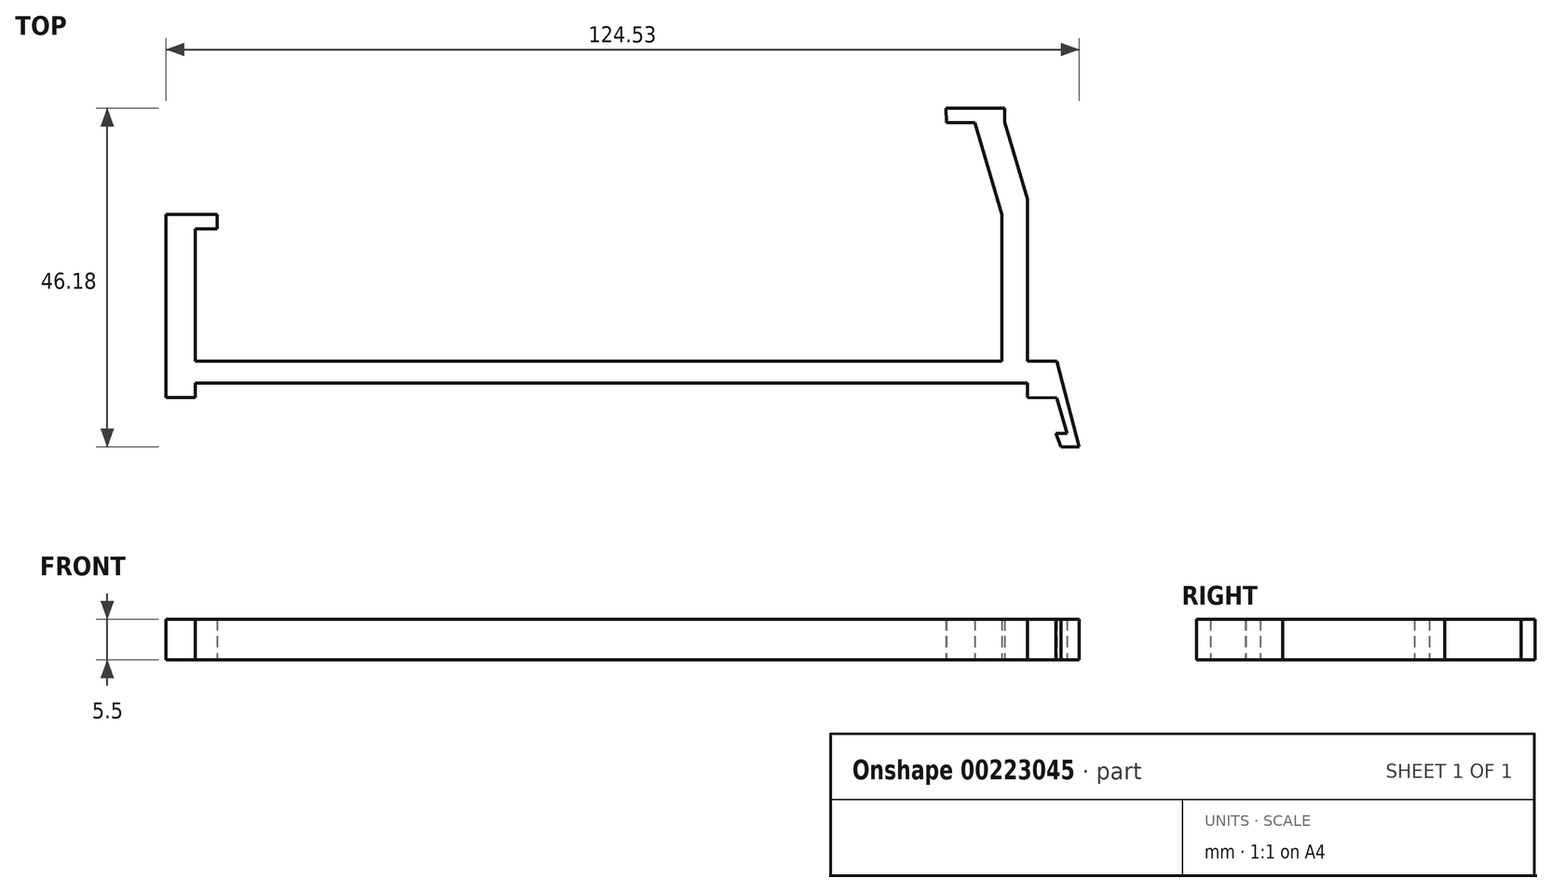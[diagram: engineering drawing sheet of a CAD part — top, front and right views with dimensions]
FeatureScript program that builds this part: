
annotation { "Feature Type Name" : "Feature", "Feature Type Description" : "" }
export const myFeature = defineFeature(function(context is Context, id is Id, definition is map)
    precondition{}
    {
        {
            var Q0;
            Q0=qCreatedBy(makeId("Top.planeOp"),FACE);
            var sketch = newSketch(context, id + "F0", { "sketchPlane" : qUnion([Q0])});
            skLineSegment(sketch, "E0.bottom", {"start": v(-40.4, -50.42) * mm, "end": v(-36.4, -50.42) * mm});
            skLineSegment(sketch, "E0.top", {"start": v(-40.4, -73.42) * mm, "end": v(-36.4, -73.42) * mm});
            skLineSegment(sketch, "E0.left", {"start": v(-40.4, -50.42) * mm, "end": v(-40.4, -73.42) * mm});
            skLineSegment(sketch, "E0.right", {"start": v(-36.4, -50.42) * mm, "end": v(-36.4, -73.42) * mm});
            skLineSegment(sketch, "E1.bottom", {"start": v(-36.4, -73.42) * mm, "end": v(77.03, -73.42) * mm});
            skLineSegment(sketch, "E1.top", {"start": v(-36.4, -70.42) * mm, "end": v(77.03, -70.42) * mm});
            skLineSegment(sketch, "E1.left", {"start": v(-36.4, -73.42) * mm, "end": v(-36.4, -70.42) * mm});
            skLineSegment(sketch, "E1.right", {"start": v(77.03, -73.42) * mm, "end": v(77.03, -70.42) * mm});
            skLineSegment(sketch, "E2.top", {"start": v(-40.4, -75.42) * mm, "end": v(-36.4, -75.42) * mm});
            skLineSegment(sketch, "E2.left", {"start": v(-40.4, -73.42) * mm, "end": v(-40.4, -75.42) * mm});
            skLineSegment(sketch, "E2.right", {"start": v(-36.4, -73.42) * mm, "end": v(-36.4, -75.42) * mm});
            skLineSegment(sketch, "E3.bottom", {"start": v(-36.4, -50.42) * mm, "end": v(-33.4, -50.42) * mm});
            skLineSegment(sketch, "E3.top", {"start": v(-36.4, -52.42) * mm, "end": v(-33.4, -52.42) * mm});
            skLineSegment(sketch, "E3.left", {"start": v(-36.4, -50.42) * mm, "end": v(-36.4, -52.42) * mm});
            skLineSegment(sketch, "E3.right", {"start": v(-33.4, -50.42) * mm, "end": v(-33.4, -52.42) * mm});
            skLineSegment(sketch, "E4.bottom", {"start": v(77.03, -70.42) * mm, "end": v(73.57, -70.42) * mm});
            skLineSegment(sketch, "E5", {"start": v(73.57, -70.42) * mm, "end": v(73.57, -50.42) * mm});
            skLineSegment(sketch, "E6", {"start": v(77.03, -70.42) * mm, "end": v(77.03, -48.3) * mm});
            skLineSegment(sketch, "E7", {"start": v(77.03, -48.3) * mm, "end": v(73.95, -37.87) * mm});
            skLineSegment(sketch, "E8", {"start": v(69.9, -37.95) * mm, "end": v(73.57, -50.42) * mm});
            skLineSegment(sketch, "E9", {"start": v(65.95, -35.95) * mm, "end": v(73.95, -35.95) * mm});
            skLineSegment(sketch, "E10", {"start": v(73.95, -35.95) * mm, "end": v(73.95, -37.87) * mm});
            skLineSegment(sketch, "E11", {"start": v(69.9, -37.95) * mm, "end": v(66, -37.95) * mm});
            skLineSegment(sketch, "E12", {"start": v(66, -37.95) * mm, "end": v(65.95, -35.95) * mm});
            skLineSegment(sketch, "E13.bottom", {"start": v(77.03, -70.42) * mm, "end": v(81.03, -70.42) * mm});
            skLineSegment(sketch, "E13.left", {"start": v(77.03, -70.42) * mm, "end": v(77.03, -73.4) * mm});
            skLineSegment(sketch, "E13.right", {"start": v(81.03, -70.42) * mm, "end": v(81.03, -73.4) * mm});
            skLineSegment(sketch, "E14", {"start": v(77.03, -73.4) * mm, "end": v(81.03, -73.4) * mm});
            skLineSegment(sketch, "E15", {"start": v(77.03, -73.4) * mm, "end": v(77.03, -75.4) * mm});
            skLineSegment(sketch, "E16", {"start": v(81.03, -73.4) * mm, "end": v(81.03, -75.45) * mm});
            skLineSegment(sketch, "E17", {"start": v(81.03, -75.45) * mm, "end": v(77.03, -75.4) * mm});
            skLineSegment(sketch, "E18", {"start": v(81.03, -75.45) * mm, "end": v(82.43, -80.25) * mm});
            skLineSegment(sketch, "E19", {"start": v(82.43, -80.25) * mm, "end": v(80.93, -80.25) * mm});
            skLineSegment(sketch, "E20", {"start": v(80.93, -80.25) * mm, "end": v(81.62, -82.13) * mm});
            skLineSegment(sketch, "E21", {"start": v(81.62, -82.13) * mm, "end": v(84.12, -82.13) * mm});
            skLineSegment(sketch, "E22", {"start": v(84.12, -82.13) * mm, "end": v(81.03, -70.42) * mm});
            skSolve(sketch);
        }
        {
            var Q0;
            Q0 = qSketchRegion(id + "F0", true);
            extrude(context, id + "F1", {"entities" : qUnion([Q0]), "depth" : 5.5 * mm});
        }
    });
